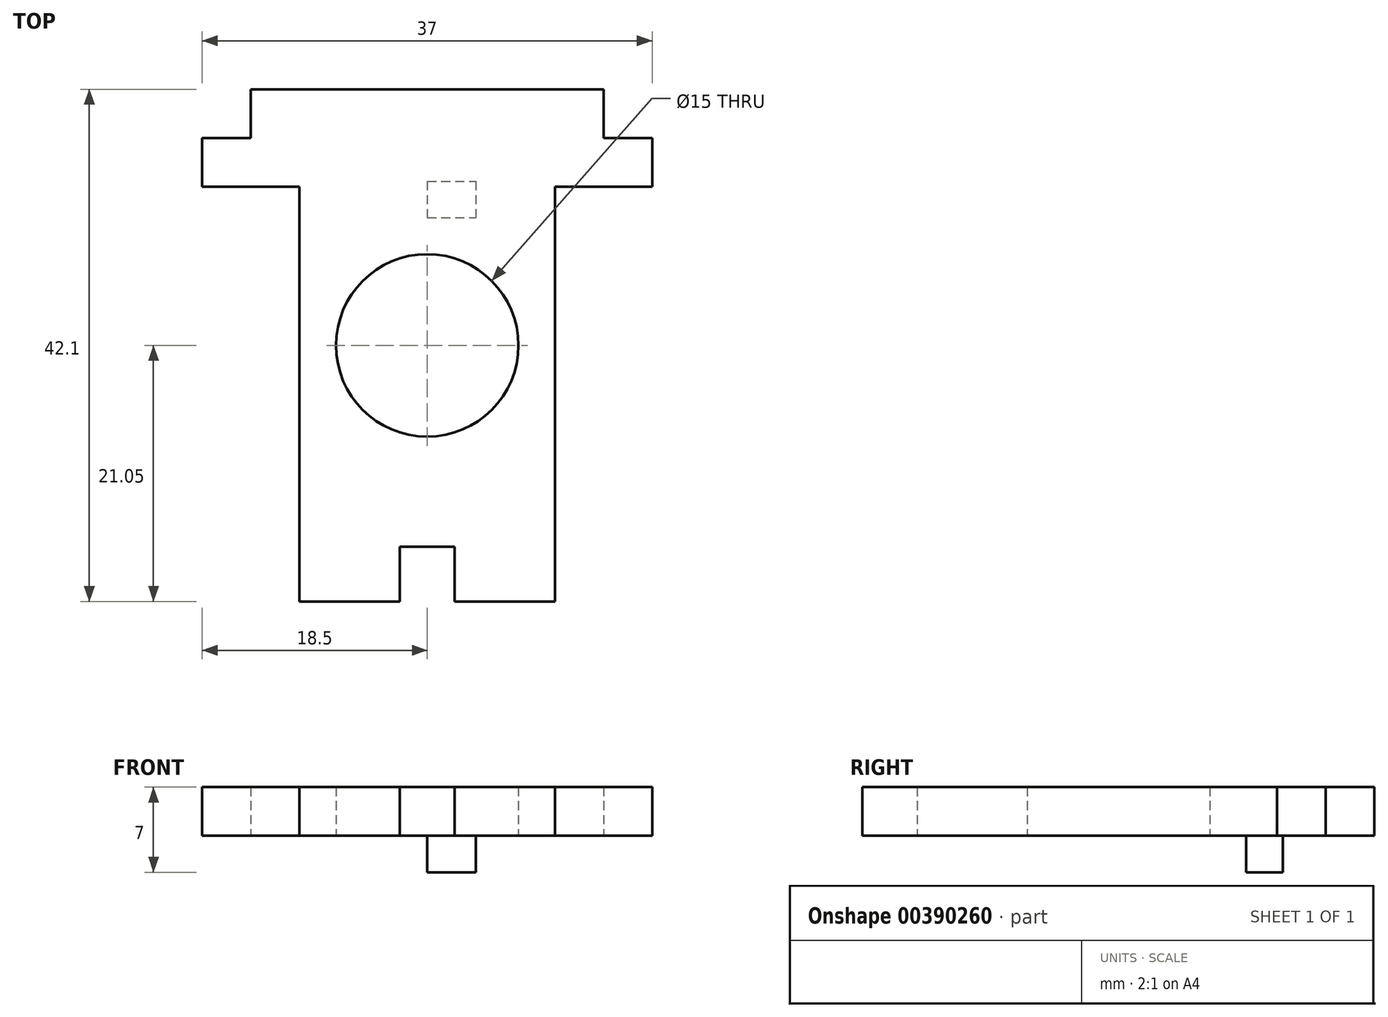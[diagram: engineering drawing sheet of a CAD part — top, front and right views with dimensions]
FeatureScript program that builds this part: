
annotation { "Feature Type Name" : "Feature", "Feature Type Description" : "" }
export const myFeature = defineFeature(function(context is Context, id is Id, definition is map)
    precondition{}
    {
        {
            var Q0;
            Q0=qCreatedBy(makeId("Top.planeOp"),FACE);
            var sketch = newSketch(context, id + "F0", { "sketchPlane" : qUnion([Q0])});
            skLineSegment(sketch, "E0.bottom", {"start": v(-10.5, 21.05) * mm, "end": v(10.5, 21.05) * mm});
            skLineSegment(sketch, "E0.top", {"start": v(-10.5, -21.05) * mm, "end": v(10.5, -21.05) * mm});
            skLineSegment(sketch, "E0.left", {"start": v(-10.5, 21.05) * mm, "end": v(-10.5, -21.05) * mm});
            skLineSegment(sketch, "E0.right", {"start": v(10.5, 21.05) * mm, "end": v(10.5, -21.05) * mm});
            skCircle(sketch, "E1", {"center": v(0, 0) * mm, "radius": 7.5 * mm});
            skLineSegment(sketch, "E2.bottom", {"start": v(2.25, -21.05) * mm, "end": v(-2.25, -21.05) * mm});
            skLineSegment(sketch, "E2.top", {"start": v(2.25, -16.55) * mm, "end": v(-2.25, -16.55) * mm});
            skLineSegment(sketch, "E2.left", {"start": v(2.25, -21.05) * mm, "end": v(2.25, -16.55) * mm});
            skLineSegment(sketch, "E2.right", {"start": v(-2.25, -21.05) * mm, "end": v(-2.25, -16.55) * mm});
            skSolve(sketch);
        }
        {
            var Q0;
            Q0=qCreatedBy(makeId("Top.planeOp"),FACE);
            var sketch = newSketch(context, id + "F1", { "sketchPlane" : qUnion([Q0])});
            skLineSegment(sketch, "E3.bottom", {"start": v(-18.5, 17.05) * mm, "end": v(18.5, 17.05) * mm});
            skLineSegment(sketch, "E3.top", {"start": v(-18.5, 13.05) * mm, "end": v(18.5, 13.05) * mm});
            skLineSegment(sketch, "E3.left", {"start": v(-18.5, 17.05) * mm, "end": v(-18.5, 13.05) * mm});
            skLineSegment(sketch, "E3.right", {"start": v(18.5, 17.05) * mm, "end": v(18.5, 13.05) * mm});
            skSolve(sketch);
        }
        {
            var Q0;
            Q0=makeQuery(id+"F0.imprint","IMPRINT",FACE,{"disambiguationData":[TD([[makeQuery(id+"F0.imprint","IMPRINT",EDGE,{"derivedFrom":sQuery(id+"F0.wireOp",EDGE,"E0.bottom")}),-1.0]])]});
            extrude(context, id + "F2", {"entities" : qUnion([Q0]), "depth" : 4 * mm});
        }
        {
            var Q0;
            Q0 = qSketchRegion(id + "F1", true);
            extrude(context, id + "F3", {"entities" : qUnion([Q0]), "operationType" : NewBodyOperationType.ADD, "depth" : 4 * mm});
        }
        {
            var Q0;
            Q0=qCreatedBy(makeId("Front.planeOp"),FACE);
            var sketch = newSketch(context, id + "F4", { "sketchPlane" : qUnion([Q0])});
            skLineSegment(sketch, "E4", {"start": v(4, 0) * mm, "end": v(4, -3) * mm});
            skLineSegment(sketch, "E5", {"start": v(4, -3) * mm, "end": v(0, -3) * mm});
            skLineSegment(sketch, "E6", {"start": v(0, -3) * mm, "end": v(0, 0) * mm});
            skLineSegment(sketch, "E7", {"start": v(0, 0) * mm, "end": v(0, 0) * mm});
            skLineSegment(sketch, "E8", {"start": v(0, 0) * mm, "end": v(4, 0) * mm});
            skLineSegment(sketch, "E9", {"start": v(4, 0) * mm, "end": v(2, 0) * mm});
            skSolve(sketch);
        }
        {
            var Q0;
            Q0 = qSketchRegion(id + "F4", true);
            extrude(context, id + "F5", {"entities" : qUnion([Q0]), "operationType" : NewBodyOperationType.ADD, "oppositeDirection" : true, "depth" : (27 / 2) * mm, "hasSecondDirection" : true, "secondDirectionOppositeDirection" : true, "secondDirectionDepth" : (27 / 2 - 3) * mm});
        }
        {
            var Q0;
            Q0=qCreatedBy(makeId("Top.planeOp"),FACE);
            var sketch = newSketch(context, id + "F6", { "sketchPlane" : qUnion([Q0])});
            skLineSegment(sketch, "E10.bottom", {"start": v(-14.5, 21.05) * mm, "end": v(14.5, 21.05) * mm});
            skLineSegment(sketch, "E10.top", {"start": v(-14.5, 13.05) * mm, "end": v(14.5, 13.05) * mm});
            skLineSegment(sketch, "E10.left", {"start": v(-14.5, 21.05) * mm, "end": v(-14.5, 13.05) * mm});
            skLineSegment(sketch, "E10.right", {"start": v(14.5, 21.05) * mm, "end": v(14.5, 13.05) * mm});
            skSolve(sketch);
        }
        {
            var Q0;
            Q0 = qSketchRegion(id + "F6", true);
            extrude(context, id + "F7", {"entities" : qUnion([Q0]), "operationType" : NewBodyOperationType.ADD, "depth" : 4 * mm});
        }
        {
            var Q0;
            Q0=qCreatedBy(makeId("Top.planeOp"),FACE);
            var sketch = newSketch(context, id + "F8", { "sketchPlane" : qUnion([Q0])});
            skLineSegment(sketch, "E11", {"start": v(-10.5, -16.55) * mm, "end": v(-4.5, -16.55) * mm, "construction": true});
            skLineSegment(sketch, "E12", {"start": v(-4.5, -16.55) * mm, "end": v(-10.5, -4) * mm, "construction": true});
            skLineSegment(sketch, "E13", {"start": v(-10.5, -16.55) * mm, "end": v(-10.5, -4) * mm, "construction": true});
            skLineSegment(sketch, "E14", {"start": v(-10.5, 4) * mm, "end": v(-10.5, 13.05) * mm, "construction": true});
            skLineSegment(sketch, "E15", {"start": v(-10.5, 13.05) * mm, "end": v(-5.02, 13.05) * mm, "construction": true});
            skLineSegment(sketch, "E16", {"start": v(-5.02, 13.05) * mm, "end": v(-10.5, 4) * mm, "construction": true});
            skSolve(sketch);
        }
        {
            var Q0;
            Q0=qCreatedBy(makeId("Top.planeOp"),FACE);
            cPlane(context, id + "F9", {"entities" : qUnion([Q0]), "cplaneType" : CPlaneType.OFFSET, "offset" : 1 * mm, "width" : 150 * mm, "height" : 150 * mm});
        }
        {
            var Q0;
            Q0=qCreatedBy(id+"F9.planeOp",FACE);
            var sketch = newSketch(context, id + "F10", { "sketchPlane" : qUnion([Q0])});
            skLineSegment(sketch, "E17", {"start": v(-7.5, -16.55) * mm, "end": v(-13.5, -4) * mm});
            skSolve(sketch);
        }
    });
